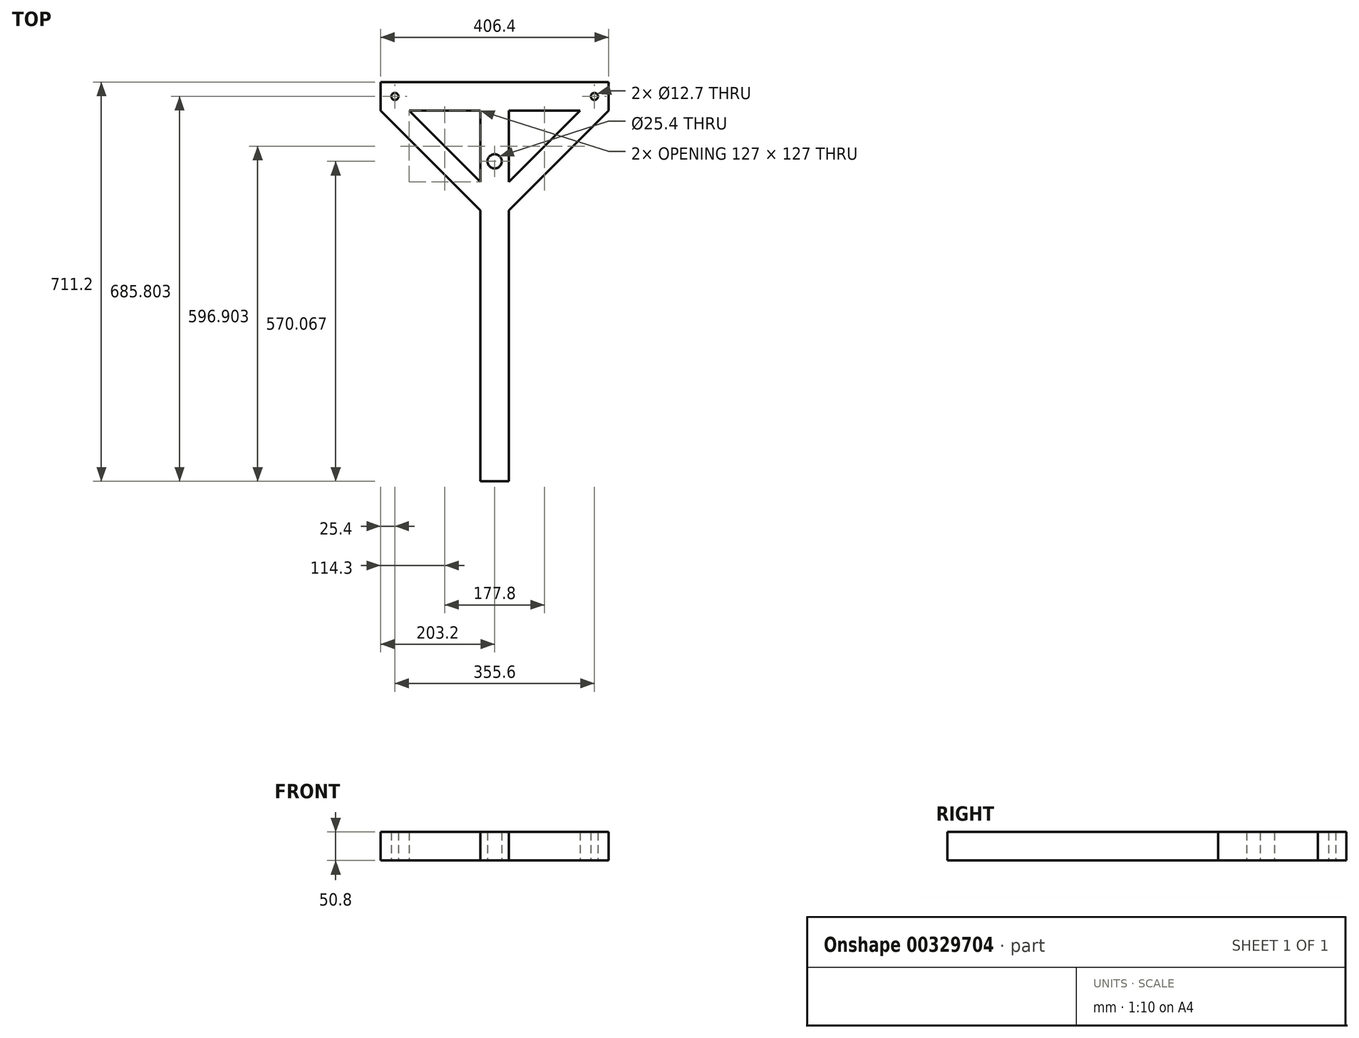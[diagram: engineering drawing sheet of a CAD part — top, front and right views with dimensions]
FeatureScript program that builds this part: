
annotation { "Feature Type Name" : "Feature", "Feature Type Description" : "" }
export const myFeature = defineFeature(function(context is Context, id is Id, definition is map)
    precondition{}
    {
        {
            var Q0;
            Q0=qCreatedBy(makeId("Top.planeOp"),FACE);
            var sketch = newSketch(context, id + "F0", { "sketchPlane" : qUnion([Q0])});
            skLineSegment(sketch, "E0.bottom", {"start": v(0, 0) * mm, "end": v(-50.8, 0) * mm});
            skLineSegment(sketch, "E0.left", {"start": v(0, 0) * mm, "end": v(0, 482.6) * mm});
            skLineSegment(sketch, "E0.right", {"start": v(-50.8, 0) * mm, "end": v(-50.8, 482.6) * mm});
            skLineSegment(sketch, "E1.bottom", {"start": v(-50.8, 660.4) * mm, "end": v(-228.6, 660.4) * mm});
            skLineSegment(sketch, "E1.top", {"start": v(-50.8, 711.2) * mm, "end": v(-228.6, 711.2) * mm});
            skLineSegment(sketch, "E1.right", {"start": v(-228.6, 660.4) * mm, "end": v(-228.6, 711.2) * mm});
            skLineSegment(sketch, "E2.bottom", {"start": v(0, 660.4) * mm, "end": v(177.8, 660.4) * mm});
            skLineSegment(sketch, "E2.top", {"start": v(0, 711.2) * mm, "end": v(177.8, 711.2) * mm});
            skLineSegment(sketch, "E2.right", {"start": v(177.8, 660.4) * mm, "end": v(177.8, 711.2) * mm});
            skLineSegment(sketch, "E3", {"start": v(-50.8, 711.2) * mm, "end": v(0, 711.2) * mm});
            skPoint(sketch, "E4.oppositeSnap0", {"position": v(-228.6, 685.8) * mm});
            skCircle(sketch, "E5", {"center": v(-203.2, 685.8) * mm, "radius": 6.35 * mm});
            skCircle(sketch, "E6", {"center": v(152.4, 685.8) * mm, "radius": 6.35 * mm});
            skLineSegment(sketch, "E7.right", {"start": v(0, 660.4) * mm, "end": v(0, 660.4) * mm});
            skLineSegment(sketch, "E8", {"start": v(-228.6, 660.4) * mm, "end": v(-50.8, 482.6) * mm});
            skLineSegment(sketch, "E9", {"start": v(0, 482.6) * mm, "end": v(177.8, 660.4) * mm});
            skLineSegment(sketch, "E10", {"start": v(-177.8, 660.4) * mm, "end": v(-50.8, 533.4) * mm});
            skLineSegment(sketch, "E11", {"start": v(127, 660.4) * mm, "end": v(0, 533.4) * mm});
            skPoint(sketch, "E11.endSnap0", {"position": v(0, 571.5) * mm});
            skLineSegment(sketch, "E12", {"start": v(-50.8, 660.4) * mm, "end": v(-50.8, 533.4) * mm});
            skLineSegment(sketch, "E13", {"start": v(0, 660.4) * mm, "end": v(0, 533.4) * mm});
            skSolve(sketch);
        }
        {
            var Q0;
            Q0 = qSketchRegion(id + "F0", true);
            extrude(context, id + "F1", {"entities" : qUnion([Q0]), "depth" : 50.8 * mm});
        }
        {
            var Q0;
            Q0=qCreatedBy(makeId("Top.planeOp"),FACE);
            var sketch = newSketch(context, id + "F2", { "sketchPlane" : qUnion([Q0])});
            skCircle(sketch, "E14", {"center": v(-25.4, 570.07) * mm, "radius": 12.7 * mm});
            skPoint(sketch, "E15.left.start.orphan", {"position": v(0, 658.97) * mm});
            skSolve(sketch);
        }
        {
            var Q0;
            Q0=sQuery(id+"F2.wireOp",VERTEX,"E14.center");
            var Q1;
            Q1=makeQuery(id+"F1.opExtrude","SWEPT_BODY",BODY,{"disambiguationData":[OSD([sQuery(id+"F0.wireOp",EDGE,"E0.bottom"),sQuery(id+"F0.wireOp",EDGE,"E0.left"),sQuery(id+"F0.wireOp",EDGE,"E0.right"),sQuery(id+"F0.wireOp",EDGE,"E1.bottom"),sQuery(id+"F0.wireOp",EDGE,"E1.top"),sQuery(id+"F0.wireOp",EDGE,"E1.right"),sQuery(id+"F0.wireOp",EDGE,"E2.bottom"),sQuery(id+"F0.wireOp",EDGE,"E2.top"),sQuery(id+"F0.wireOp",EDGE,"E2.right"),sQuery(id+"F0.wireOp",EDGE,"E3"),sQuery(id+"F0.wireOp",EDGE,"E5"),sQuery(id+"F0.wireOp",EDGE,"E6"),sQuery(id+"F0.wireOp",EDGE,"E8"),sQuery(id+"F0.wireOp",EDGE,"E9"),sQuery(id+"F0.wireOp",EDGE,"E10"),sQuery(id+"F0.wireOp",EDGE,"E11"),sQuery(id+"F0.wireOp",EDGE,"E12"),sQuery(id+"F0.wireOp",EDGE,"E13")])]});
            hole(context, id + "F3", {"style" : HoleStyle.SIMPLE, "endStyle" : HoleEndStyle.THROUGH, "oppositeDirection" : true, "holeDiameter" : 25.4 * mm, "tappedDepth" : 12.7 * mm, "tapClearance" : 3, "locations" : qUnion([Q0]), "scope" : qUnion([Q1])});
        }
    });
